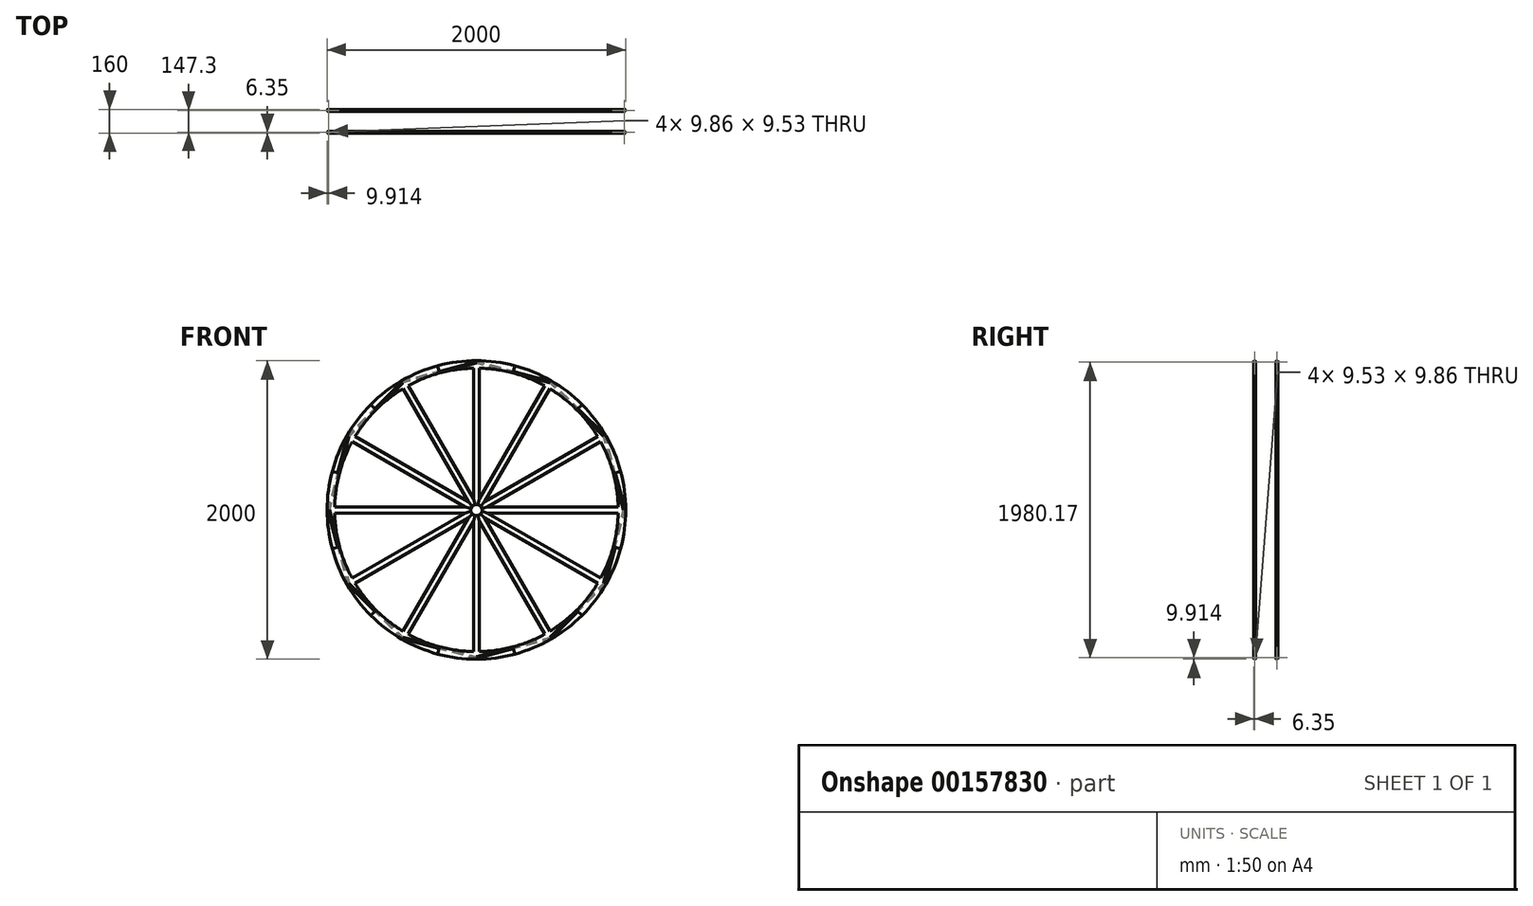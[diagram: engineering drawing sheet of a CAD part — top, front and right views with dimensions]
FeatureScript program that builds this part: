
annotation { "Feature Type Name" : "Feature", "Feature Type Description" : "" }
export const myFeature = defineFeature(function(context is Context, id is Id, definition is map)
    precondition{}
    {
        {
            var Q0;
            Q0=qCreatedBy(makeId("Front.planeOp"),FACE);
            var sketch = newSketch(context, id + "F0", { "sketchPlane" : qUnion([Q0])});
            skLineSegment(sketch, "E0", {"start": v(0, 0) * mm, "end": v(1000, 0) * mm, "construction": true});
            skCircle(sketch, "E1", {"center": v(0, 0) * mm, "radius": 1000 * mm, "construction": true});
            skLineSegment(sketch, "E2", {"start": v(0, 0) * mm, "end": v(965.93, 258.82) * mm, "construction": true});
            skCircle(sketch, "E3", {"center": v(0, 0) * mm, "radius": 77.27 * mm, "construction": true});
            skLineSegment(sketch, "E4", {"start": v(37.32, 10) * mm, "end": v(37.32, 0) * mm});
            skLineSegment(sketch, "E5", {"start": v(37.32, 10) * mm, "end": v(74.64, 20) * mm});
            skLineSegment(sketch, "E6", {"start": v(74.64, 20) * mm, "end": v(949.79, 20) * mm});
            skArc(sketch, "E7", {"start": v(1000, 0) * mm, "mid": v(991.44, 130.53) * mm, "end": v(965.93, 258.82) * mm});
            skArc(sketch, "E8", {"start": v(949.79, 20) * mm, "mid": v(940.52, 133.9) * mm, "end": v(917.63, 245.88) * mm});
            skLineSegment(sketch, "E9", {"start": v(917.63, 245.88) * mm, "end": v(965.93, 258.82) * mm});
            skArc(sketch, "E10.MirrorCS", {"start": v(1000, 0) * mm, "mid": v(991.44, -130.53) * mm, "end": v(965.93, -258.82) * mm});
            skLineSegment(sketch, "E11.MirrorCS", {"start": v(917.63, -245.88) * mm, "end": v(965.93, -258.82) * mm});
            skArc(sketch, "E12.MirrorCS", {"start": v(949.79, -20) * mm, "mid": v(940.52, -133.9) * mm, "end": v(917.63, -245.88) * mm});
            skLineSegment(sketch, "E13.MirrorCS", {"start": v(74.64, -20) * mm, "end": v(949.79, -20) * mm});
            skLineSegment(sketch, "E14.MirrorCS", {"start": v(37.32, -10) * mm, "end": v(37.32, 0) * mm});
            skLineSegment(sketch, "E15.MirrorCS", {"start": v(37.32, -10) * mm, "end": v(74.64, -20) * mm});
            skSolve(sketch);
        }
        {
            var Q0;
            Q0=makeQuery(id+"F0.imprint","IMPRINT",FACE,{"disambiguationData":[TD([[makeQuery(id+"F0.imprint","IMPRINT",EDGE,{"derivedFrom":sQuery(id+"F0.wireOp",EDGE,"E4")}),1.0]])]});
            extrude(context, id + "F1", {"entities" : qUnion([Q0]), "depth" : 1 / 406.4 * mm});
        }
        {
            var Q0;
            Q0=qCreatedBy(makeId("Right.planeOp"),FACE);
            var sketch = newSketch(context, id + "F2", { "sketchPlane" : qUnion([Q0])});
            skLineSegment(sketch, "E16", {"start": v(0, 0) * mm, "end": v(504.9, 0) * mm, "construction": true});
            skSolve(sketch);
        }
        {
            var Q0;
            Q0=sQuery(id+"F0.wireOp",VERTEX,"E7.end");
            var Q1;
            Q1=sQuery(id+"F0.wireOp",EDGE,"E1");
            cPlane(context, id + "F3", {"entities" : qUnion([Q0, Q1]), "cplaneType" : CPlaneType.CURVE_POINT, "offset" : 25 * mm, "width" : 150 * mm, "height" : 150 * mm});
        }
        {
            var Q0;
            Q0=qCreatedBy(id+"F3.planeOp",FACE);
            var sketch = newSketch(context, id + "F4", { "sketchPlane" : qUnion([Q0])});
            skLineSegment(sketch, "E17.bottom", {"start": v(950.5, 0) * mm, "end": v(962.2, 0) * mm});
            skLineSegment(sketch, "E17.top", {"start": v(950.5, 12.7) * mm, "end": v(962.2, 12.7) * mm});
            skLineSegment(sketch, "E17.left", {"start": v(950, 0.5) * mm, "end": v(950, 12.2) * mm});
            skLineSegment(sketch, "E17.right", {"start": v(962.7, 0.5) * mm, "end": v(962.7, 12.2) * mm});
            skLineSegment(sketch, "E18.0", {"start": v(951.59, 1.59) * mm, "end": v(951.59, 11.11) * mm});
            skLineSegment(sketch, "E18.1", {"start": v(951.59, 1.59) * mm, "end": v(961.11, 1.59) * mm});
            skLineSegment(sketch, "E18.2", {"start": v(961.11, 1.59) * mm, "end": v(961.11, 11.11) * mm});
            skLineSegment(sketch, "E18.3", {"start": v(951.59, 11.11) * mm, "end": v(961.11, 11.11) * mm});
            skPoint(sketch, "E19.visualSharp", {"position": v(950, 12.7) * mm});
            skArc(sketch, "E19.filletArc", {"start": v(950.5, 12.7) * mm, "mid": v(950.15, 12.55) * mm, "end": v(950, 12.2) * mm});
            skPoint(sketch, "E20.visualSharp", {"position": v(962.7, 12.7) * mm});
            skArc(sketch, "E20.filletArc", {"start": v(962.7, 12.2) * mm, "mid": v(962.55, 12.55) * mm, "end": v(962.2, 12.7) * mm});
            skPoint(sketch, "E21.visualSharp", {"position": v(962.7, 0) * mm});
            skArc(sketch, "E21.filletArc", {"start": v(962.2, 0) * mm, "mid": v(962.55, 0.15) * mm, "end": v(962.7, 0.5) * mm});
            skPoint(sketch, "E22.visualSharp", {"position": v(950, 0) * mm});
            skArc(sketch, "E22.filletArc", {"start": v(950, 0.5) * mm, "mid": v(950.15, 0.15) * mm, "end": v(950.5, 0) * mm});
            skSolve(sketch);
        }
        {
            var Q0;
            Q0 = qSketchRegion(id + "F4", true);
            var Q1;
            Q1=qCreatedBy(makeId("Top.planeOp"),FACE);
            extrude(context, id + "F5", {"entities" : qUnion([Q0]), "endBound" : BoundingType.UP_TO_SURFACE, "oppositeDirection" : true, "endBoundEntityFace" : qUnion([Q1]), "depth" : 25 * mm});
        }
        {
            var Q0;
            Q0=makeQuery(id+"F5.opExtrude","SWEPT_BODY",BODY,{"disambiguationData":[OSD([sQuery(id+"F4.wireOp",EDGE,"E17.bottom"),sQuery(id+"F4.wireOp",EDGE,"E17.top"),sQuery(id+"F4.wireOp",EDGE,"E17.left"),sQuery(id+"F4.wireOp",EDGE,"E17.right"),sQuery(id+"F4.wireOp",EDGE,"E18.0"),sQuery(id+"F4.wireOp",EDGE,"E18.1"),sQuery(id+"F4.wireOp",EDGE,"E18.2"),sQuery(id+"F4.wireOp",EDGE,"E18.3"),sQuery(id+"F4.wireOp",EDGE,"E19.filletArc"),sQuery(id+"F4.wireOp",EDGE,"E20.filletArc"),sQuery(id+"F4.wireOp",EDGE,"E21.filletArc"),sQuery(id+"F4.wireOp",EDGE,"E22.filletArc")])]});
            var Q1;
            Q1=qCreatedBy(id+"F3.planeOp",FACE);
            mirror(context, id + "F6", {"operationType" : NewBodyOperationType.ADD, "entities" : qUnion([Q0]), "mirrorPlane" : qUnion([Q1])});
        }
        {
            var Q0;
            Q0=makeQuery(id+"F1.opExtrude","SWEPT_BODY",BODY,{"disambiguationData":[OSD([sQuery(id+"F0.wireOp",EDGE,"E4"),sQuery(id+"F0.wireOp",EDGE,"E5"),sQuery(id+"F0.wireOp",EDGE,"E6"),sQuery(id+"F0.wireOp",EDGE,"E7"),sQuery(id+"F0.wireOp",EDGE,"E8"),sQuery(id+"F0.wireOp",EDGE,"E9"),sQuery(id+"F0.wireOp",EDGE,"E10.MirrorCS"),sQuery(id+"F0.wireOp",EDGE,"E11.MirrorCS"),sQuery(id+"F0.wireOp",EDGE,"E12.MirrorCS"),sQuery(id+"F0.wireOp",EDGE,"E13.MirrorCS"),sQuery(id+"F0.wireOp",EDGE,"E14.MirrorCS"),sQuery(id+"F0.wireOp",EDGE,"E15.MirrorCS")])]});
            var Q1;
            Q1=makeQuery(id+"F5.opExtrude","SWEPT_BODY",BODY,{"disambiguationData":[OSD([sQuery(id+"F4.wireOp",EDGE,"E17.bottom"),sQuery(id+"F4.wireOp",EDGE,"E17.top"),sQuery(id+"F4.wireOp",EDGE,"E17.left"),sQuery(id+"F4.wireOp",EDGE,"E17.right"),sQuery(id+"F4.wireOp",EDGE,"E18.0"),sQuery(id+"F4.wireOp",EDGE,"E18.1"),sQuery(id+"F4.wireOp",EDGE,"E18.2"),sQuery(id+"F4.wireOp",EDGE,"E18.3"),sQuery(id+"F4.wireOp",EDGE,"E19.filletArc"),sQuery(id+"F4.wireOp",EDGE,"E20.filletArc"),sQuery(id+"F4.wireOp",EDGE,"E21.filletArc"),sQuery(id+"F4.wireOp",EDGE,"E22.filletArc")])]});
            var Q2;
            Q2=sQuery(id+"F2.wireOp",EDGE,"E16");
            circularPattern(context, id + "F7", {"entities" : qUnion([Q0, Q1]), "axis" : qUnion([Q2]), "angle" : 30 * degree, "instanceCount" : 12});
        }
        {
            var Q0;
            Q0=qCreatedBy(makeId("Front.planeOp"),FACE);
            cPlane(context, id + "F8", {"entities" : qUnion([Q0]), "cplaneType" : CPlaneType.OFFSET, "offset" : 80 * mm, "oppositeDirection" : true, "width" : 150 * mm, "height" : 150 * mm});
        }
        {
            var Q0;
            Q0=makeQuery(id+"F1.opExtrude","SWEPT_BODY",BODY,{"disambiguationData":[OSD([sQuery(id+"F0.wireOp",EDGE,"E4"),sQuery(id+"F0.wireOp",EDGE,"E5"),sQuery(id+"F0.wireOp",EDGE,"E6"),sQuery(id+"F0.wireOp",EDGE,"E7"),sQuery(id+"F0.wireOp",EDGE,"E8"),sQuery(id+"F0.wireOp",EDGE,"E9"),sQuery(id+"F0.wireOp",EDGE,"E10.MirrorCS"),sQuery(id+"F0.wireOp",EDGE,"E11.MirrorCS"),sQuery(id+"F0.wireOp",EDGE,"E12.MirrorCS"),sQuery(id+"F0.wireOp",EDGE,"E13.MirrorCS"),sQuery(id+"F0.wireOp",EDGE,"E14.MirrorCS"),sQuery(id+"F0.wireOp",EDGE,"E15.MirrorCS")])]});
            var Q1;
            Q1=makeQuery(id+"F5.opExtrude","SWEPT_BODY",BODY,{"disambiguationData":[OSD([sQuery(id+"F4.wireOp",EDGE,"E17.bottom"),sQuery(id+"F4.wireOp",EDGE,"E17.top"),sQuery(id+"F4.wireOp",EDGE,"E17.left"),sQuery(id+"F4.wireOp",EDGE,"E17.right"),sQuery(id+"F4.wireOp",EDGE,"E18.0"),sQuery(id+"F4.wireOp",EDGE,"E18.1"),sQuery(id+"F4.wireOp",EDGE,"E18.2"),sQuery(id+"F4.wireOp",EDGE,"E18.3"),sQuery(id+"F4.wireOp",EDGE,"E19.filletArc"),sQuery(id+"F4.wireOp",EDGE,"E20.filletArc"),sQuery(id+"F4.wireOp",EDGE,"E21.filletArc"),sQuery(id+"F4.wireOp",EDGE,"E22.filletArc")])]});
            var Q2;
            Q2=makeQuery(id+"F7.opPattern","COPY",BODY,{"derivedFrom":makeQuery(id+"F1.opExtrude","SWEPT_BODY",BODY,{"disambiguationData":[OSD([sQuery(id+"F0.wireOp",EDGE,"E4"),sQuery(id+"F0.wireOp",EDGE,"E5"),sQuery(id+"F0.wireOp",EDGE,"E6"),sQuery(id+"F0.wireOp",EDGE,"E7"),sQuery(id+"F0.wireOp",EDGE,"E8"),sQuery(id+"F0.wireOp",EDGE,"E9"),sQuery(id+"F0.wireOp",EDGE,"E10.MirrorCS"),sQuery(id+"F0.wireOp",EDGE,"E11.MirrorCS"),sQuery(id+"F0.wireOp",EDGE,"E12.MirrorCS"),sQuery(id+"F0.wireOp",EDGE,"E13.MirrorCS"),sQuery(id+"F0.wireOp",EDGE,"E14.MirrorCS"),sQuery(id+"F0.wireOp",EDGE,"E15.MirrorCS")])]}),"instanceName":"1"});
            var Q3;
            Q3=makeQuery(id+"F7.opPattern","COPY",BODY,{"derivedFrom":makeQuery(id+"F5.opExtrude","SWEPT_BODY",BODY,{"disambiguationData":[OSD([sQuery(id+"F4.wireOp",EDGE,"E17.bottom"),sQuery(id+"F4.wireOp",EDGE,"E17.top"),sQuery(id+"F4.wireOp",EDGE,"E17.left"),sQuery(id+"F4.wireOp",EDGE,"E17.right"),sQuery(id+"F4.wireOp",EDGE,"E18.0"),sQuery(id+"F4.wireOp",EDGE,"E18.1"),sQuery(id+"F4.wireOp",EDGE,"E18.2"),sQuery(id+"F4.wireOp",EDGE,"E18.3"),sQuery(id+"F4.wireOp",EDGE,"E19.filletArc"),sQuery(id+"F4.wireOp",EDGE,"E20.filletArc"),sQuery(id+"F4.wireOp",EDGE,"E21.filletArc"),sQuery(id+"F4.wireOp",EDGE,"E22.filletArc")])]}),"instanceName":"1"});
            var Q4;
            Q4=makeQuery(id+"F7.opPattern","COPY",BODY,{"derivedFrom":makeQuery(id+"F1.opExtrude","SWEPT_BODY",BODY,{"disambiguationData":[OSD([sQuery(id+"F0.wireOp",EDGE,"E4"),sQuery(id+"F0.wireOp",EDGE,"E5"),sQuery(id+"F0.wireOp",EDGE,"E6"),sQuery(id+"F0.wireOp",EDGE,"E7"),sQuery(id+"F0.wireOp",EDGE,"E8"),sQuery(id+"F0.wireOp",EDGE,"E9"),sQuery(id+"F0.wireOp",EDGE,"E10.MirrorCS"),sQuery(id+"F0.wireOp",EDGE,"E11.MirrorCS"),sQuery(id+"F0.wireOp",EDGE,"E12.MirrorCS"),sQuery(id+"F0.wireOp",EDGE,"E13.MirrorCS"),sQuery(id+"F0.wireOp",EDGE,"E14.MirrorCS"),sQuery(id+"F0.wireOp",EDGE,"E15.MirrorCS")])]}),"instanceName":"2"});
            var Q5;
            Q5=makeQuery(id+"F7.opPattern","COPY",BODY,{"derivedFrom":makeQuery(id+"F5.opExtrude","SWEPT_BODY",BODY,{"disambiguationData":[OSD([sQuery(id+"F4.wireOp",EDGE,"E17.bottom"),sQuery(id+"F4.wireOp",EDGE,"E17.top"),sQuery(id+"F4.wireOp",EDGE,"E17.left"),sQuery(id+"F4.wireOp",EDGE,"E17.right"),sQuery(id+"F4.wireOp",EDGE,"E18.0"),sQuery(id+"F4.wireOp",EDGE,"E18.1"),sQuery(id+"F4.wireOp",EDGE,"E18.2"),sQuery(id+"F4.wireOp",EDGE,"E18.3"),sQuery(id+"F4.wireOp",EDGE,"E19.filletArc"),sQuery(id+"F4.wireOp",EDGE,"E20.filletArc"),sQuery(id+"F4.wireOp",EDGE,"E21.filletArc"),sQuery(id+"F4.wireOp",EDGE,"E22.filletArc")])]}),"instanceName":"2"});
            var Q6;
            Q6=makeQuery(id+"F7.opPattern","COPY",BODY,{"derivedFrom":makeQuery(id+"F1.opExtrude","SWEPT_BODY",BODY,{"disambiguationData":[OSD([sQuery(id+"F0.wireOp",EDGE,"E4"),sQuery(id+"F0.wireOp",EDGE,"E5"),sQuery(id+"F0.wireOp",EDGE,"E6"),sQuery(id+"F0.wireOp",EDGE,"E7"),sQuery(id+"F0.wireOp",EDGE,"E8"),sQuery(id+"F0.wireOp",EDGE,"E9"),sQuery(id+"F0.wireOp",EDGE,"E10.MirrorCS"),sQuery(id+"F0.wireOp",EDGE,"E11.MirrorCS"),sQuery(id+"F0.wireOp",EDGE,"E12.MirrorCS"),sQuery(id+"F0.wireOp",EDGE,"E13.MirrorCS"),sQuery(id+"F0.wireOp",EDGE,"E14.MirrorCS"),sQuery(id+"F0.wireOp",EDGE,"E15.MirrorCS")])]}),"instanceName":"3"});
            var Q7;
            Q7=makeQuery(id+"F7.opPattern","COPY",BODY,{"derivedFrom":makeQuery(id+"F5.opExtrude","SWEPT_BODY",BODY,{"disambiguationData":[OSD([sQuery(id+"F4.wireOp",EDGE,"E17.bottom"),sQuery(id+"F4.wireOp",EDGE,"E17.top"),sQuery(id+"F4.wireOp",EDGE,"E17.left"),sQuery(id+"F4.wireOp",EDGE,"E17.right"),sQuery(id+"F4.wireOp",EDGE,"E18.0"),sQuery(id+"F4.wireOp",EDGE,"E18.1"),sQuery(id+"F4.wireOp",EDGE,"E18.2"),sQuery(id+"F4.wireOp",EDGE,"E18.3"),sQuery(id+"F4.wireOp",EDGE,"E19.filletArc"),sQuery(id+"F4.wireOp",EDGE,"E20.filletArc"),sQuery(id+"F4.wireOp",EDGE,"E21.filletArc"),sQuery(id+"F4.wireOp",EDGE,"E22.filletArc")])]}),"instanceName":"3"});
            var Q8;
            Q8=makeQuery(id+"F7.opPattern","COPY",BODY,{"derivedFrom":makeQuery(id+"F1.opExtrude","SWEPT_BODY",BODY,{"disambiguationData":[OSD([sQuery(id+"F0.wireOp",EDGE,"E4"),sQuery(id+"F0.wireOp",EDGE,"E5"),sQuery(id+"F0.wireOp",EDGE,"E6"),sQuery(id+"F0.wireOp",EDGE,"E7"),sQuery(id+"F0.wireOp",EDGE,"E8"),sQuery(id+"F0.wireOp",EDGE,"E9"),sQuery(id+"F0.wireOp",EDGE,"E10.MirrorCS"),sQuery(id+"F0.wireOp",EDGE,"E11.MirrorCS"),sQuery(id+"F0.wireOp",EDGE,"E12.MirrorCS"),sQuery(id+"F0.wireOp",EDGE,"E13.MirrorCS"),sQuery(id+"F0.wireOp",EDGE,"E14.MirrorCS"),sQuery(id+"F0.wireOp",EDGE,"E15.MirrorCS")])]}),"instanceName":"4"});
            var Q9;
            Q9=makeQuery(id+"F7.opPattern","COPY",BODY,{"derivedFrom":makeQuery(id+"F5.opExtrude","SWEPT_BODY",BODY,{"disambiguationData":[OSD([sQuery(id+"F4.wireOp",EDGE,"E17.bottom"),sQuery(id+"F4.wireOp",EDGE,"E17.top"),sQuery(id+"F4.wireOp",EDGE,"E17.left"),sQuery(id+"F4.wireOp",EDGE,"E17.right"),sQuery(id+"F4.wireOp",EDGE,"E18.0"),sQuery(id+"F4.wireOp",EDGE,"E18.1"),sQuery(id+"F4.wireOp",EDGE,"E18.2"),sQuery(id+"F4.wireOp",EDGE,"E18.3"),sQuery(id+"F4.wireOp",EDGE,"E19.filletArc"),sQuery(id+"F4.wireOp",EDGE,"E20.filletArc"),sQuery(id+"F4.wireOp",EDGE,"E21.filletArc"),sQuery(id+"F4.wireOp",EDGE,"E22.filletArc")])]}),"instanceName":"4"});
            var Q10;
            Q10=makeQuery(id+"F7.opPattern","COPY",BODY,{"derivedFrom":makeQuery(id+"F1.opExtrude","SWEPT_BODY",BODY,{"disambiguationData":[OSD([sQuery(id+"F0.wireOp",EDGE,"E4"),sQuery(id+"F0.wireOp",EDGE,"E5"),sQuery(id+"F0.wireOp",EDGE,"E6"),sQuery(id+"F0.wireOp",EDGE,"E7"),sQuery(id+"F0.wireOp",EDGE,"E8"),sQuery(id+"F0.wireOp",EDGE,"E9"),sQuery(id+"F0.wireOp",EDGE,"E10.MirrorCS"),sQuery(id+"F0.wireOp",EDGE,"E11.MirrorCS"),sQuery(id+"F0.wireOp",EDGE,"E12.MirrorCS"),sQuery(id+"F0.wireOp",EDGE,"E13.MirrorCS"),sQuery(id+"F0.wireOp",EDGE,"E14.MirrorCS"),sQuery(id+"F0.wireOp",EDGE,"E15.MirrorCS")])]}),"instanceName":"5"});
            var Q11;
            Q11=makeQuery(id+"F7.opPattern","COPY",BODY,{"derivedFrom":makeQuery(id+"F5.opExtrude","SWEPT_BODY",BODY,{"disambiguationData":[OSD([sQuery(id+"F4.wireOp",EDGE,"E17.bottom"),sQuery(id+"F4.wireOp",EDGE,"E17.top"),sQuery(id+"F4.wireOp",EDGE,"E17.left"),sQuery(id+"F4.wireOp",EDGE,"E17.right"),sQuery(id+"F4.wireOp",EDGE,"E18.0"),sQuery(id+"F4.wireOp",EDGE,"E18.1"),sQuery(id+"F4.wireOp",EDGE,"E18.2"),sQuery(id+"F4.wireOp",EDGE,"E18.3"),sQuery(id+"F4.wireOp",EDGE,"E19.filletArc"),sQuery(id+"F4.wireOp",EDGE,"E20.filletArc"),sQuery(id+"F4.wireOp",EDGE,"E21.filletArc"),sQuery(id+"F4.wireOp",EDGE,"E22.filletArc")])]}),"instanceName":"5"});
            var Q12;
            Q12=makeQuery(id+"F7.opPattern","COPY",BODY,{"derivedFrom":makeQuery(id+"F1.opExtrude","SWEPT_BODY",BODY,{"disambiguationData":[OSD([sQuery(id+"F0.wireOp",EDGE,"E4"),sQuery(id+"F0.wireOp",EDGE,"E5"),sQuery(id+"F0.wireOp",EDGE,"E6"),sQuery(id+"F0.wireOp",EDGE,"E7"),sQuery(id+"F0.wireOp",EDGE,"E8"),sQuery(id+"F0.wireOp",EDGE,"E9"),sQuery(id+"F0.wireOp",EDGE,"E10.MirrorCS"),sQuery(id+"F0.wireOp",EDGE,"E11.MirrorCS"),sQuery(id+"F0.wireOp",EDGE,"E12.MirrorCS"),sQuery(id+"F0.wireOp",EDGE,"E13.MirrorCS"),sQuery(id+"F0.wireOp",EDGE,"E14.MirrorCS"),sQuery(id+"F0.wireOp",EDGE,"E15.MirrorCS")])]}),"instanceName":"6"});
            var Q13;
            Q13=makeQuery(id+"F7.opPattern","COPY",BODY,{"derivedFrom":makeQuery(id+"F5.opExtrude","SWEPT_BODY",BODY,{"disambiguationData":[OSD([sQuery(id+"F4.wireOp",EDGE,"E17.bottom"),sQuery(id+"F4.wireOp",EDGE,"E17.top"),sQuery(id+"F4.wireOp",EDGE,"E17.left"),sQuery(id+"F4.wireOp",EDGE,"E17.right"),sQuery(id+"F4.wireOp",EDGE,"E18.0"),sQuery(id+"F4.wireOp",EDGE,"E18.1"),sQuery(id+"F4.wireOp",EDGE,"E18.2"),sQuery(id+"F4.wireOp",EDGE,"E18.3"),sQuery(id+"F4.wireOp",EDGE,"E19.filletArc"),sQuery(id+"F4.wireOp",EDGE,"E20.filletArc"),sQuery(id+"F4.wireOp",EDGE,"E21.filletArc"),sQuery(id+"F4.wireOp",EDGE,"E22.filletArc")])]}),"instanceName":"6"});
            var Q14;
            Q14=makeQuery(id+"F7.opPattern","COPY",BODY,{"derivedFrom":makeQuery(id+"F1.opExtrude","SWEPT_BODY",BODY,{"disambiguationData":[OSD([sQuery(id+"F0.wireOp",EDGE,"E4"),sQuery(id+"F0.wireOp",EDGE,"E5"),sQuery(id+"F0.wireOp",EDGE,"E6"),sQuery(id+"F0.wireOp",EDGE,"E7"),sQuery(id+"F0.wireOp",EDGE,"E8"),sQuery(id+"F0.wireOp",EDGE,"E9"),sQuery(id+"F0.wireOp",EDGE,"E10.MirrorCS"),sQuery(id+"F0.wireOp",EDGE,"E11.MirrorCS"),sQuery(id+"F0.wireOp",EDGE,"E12.MirrorCS"),sQuery(id+"F0.wireOp",EDGE,"E13.MirrorCS"),sQuery(id+"F0.wireOp",EDGE,"E14.MirrorCS"),sQuery(id+"F0.wireOp",EDGE,"E15.MirrorCS")])]}),"instanceName":"7"});
            var Q15;
            Q15=makeQuery(id+"F7.opPattern","COPY",BODY,{"derivedFrom":makeQuery(id+"F5.opExtrude","SWEPT_BODY",BODY,{"disambiguationData":[OSD([sQuery(id+"F4.wireOp",EDGE,"E17.bottom"),sQuery(id+"F4.wireOp",EDGE,"E17.top"),sQuery(id+"F4.wireOp",EDGE,"E17.left"),sQuery(id+"F4.wireOp",EDGE,"E17.right"),sQuery(id+"F4.wireOp",EDGE,"E18.0"),sQuery(id+"F4.wireOp",EDGE,"E18.1"),sQuery(id+"F4.wireOp",EDGE,"E18.2"),sQuery(id+"F4.wireOp",EDGE,"E18.3"),sQuery(id+"F4.wireOp",EDGE,"E19.filletArc"),sQuery(id+"F4.wireOp",EDGE,"E20.filletArc"),sQuery(id+"F4.wireOp",EDGE,"E21.filletArc"),sQuery(id+"F4.wireOp",EDGE,"E22.filletArc")])]}),"instanceName":"7"});
            var Q16;
            Q16=makeQuery(id+"F7.opPattern","COPY",BODY,{"derivedFrom":makeQuery(id+"F1.opExtrude","SWEPT_BODY",BODY,{"disambiguationData":[OSD([sQuery(id+"F0.wireOp",EDGE,"E4"),sQuery(id+"F0.wireOp",EDGE,"E5"),sQuery(id+"F0.wireOp",EDGE,"E6"),sQuery(id+"F0.wireOp",EDGE,"E7"),sQuery(id+"F0.wireOp",EDGE,"E8"),sQuery(id+"F0.wireOp",EDGE,"E9"),sQuery(id+"F0.wireOp",EDGE,"E10.MirrorCS"),sQuery(id+"F0.wireOp",EDGE,"E11.MirrorCS"),sQuery(id+"F0.wireOp",EDGE,"E12.MirrorCS"),sQuery(id+"F0.wireOp",EDGE,"E13.MirrorCS"),sQuery(id+"F0.wireOp",EDGE,"E14.MirrorCS"),sQuery(id+"F0.wireOp",EDGE,"E15.MirrorCS")])]}),"instanceName":"8"});
            var Q17;
            Q17=makeQuery(id+"F7.opPattern","COPY",BODY,{"derivedFrom":makeQuery(id+"F5.opExtrude","SWEPT_BODY",BODY,{"disambiguationData":[OSD([sQuery(id+"F4.wireOp",EDGE,"E17.bottom"),sQuery(id+"F4.wireOp",EDGE,"E17.top"),sQuery(id+"F4.wireOp",EDGE,"E17.left"),sQuery(id+"F4.wireOp",EDGE,"E17.right"),sQuery(id+"F4.wireOp",EDGE,"E18.0"),sQuery(id+"F4.wireOp",EDGE,"E18.1"),sQuery(id+"F4.wireOp",EDGE,"E18.2"),sQuery(id+"F4.wireOp",EDGE,"E18.3"),sQuery(id+"F4.wireOp",EDGE,"E19.filletArc"),sQuery(id+"F4.wireOp",EDGE,"E20.filletArc"),sQuery(id+"F4.wireOp",EDGE,"E21.filletArc"),sQuery(id+"F4.wireOp",EDGE,"E22.filletArc")])]}),"instanceName":"8"});
            var Q18;
            Q18=makeQuery(id+"F7.opPattern","COPY",BODY,{"derivedFrom":makeQuery(id+"F1.opExtrude","SWEPT_BODY",BODY,{"disambiguationData":[OSD([sQuery(id+"F0.wireOp",EDGE,"E4"),sQuery(id+"F0.wireOp",EDGE,"E5"),sQuery(id+"F0.wireOp",EDGE,"E6"),sQuery(id+"F0.wireOp",EDGE,"E7"),sQuery(id+"F0.wireOp",EDGE,"E8"),sQuery(id+"F0.wireOp",EDGE,"E9"),sQuery(id+"F0.wireOp",EDGE,"E10.MirrorCS"),sQuery(id+"F0.wireOp",EDGE,"E11.MirrorCS"),sQuery(id+"F0.wireOp",EDGE,"E12.MirrorCS"),sQuery(id+"F0.wireOp",EDGE,"E13.MirrorCS"),sQuery(id+"F0.wireOp",EDGE,"E14.MirrorCS"),sQuery(id+"F0.wireOp",EDGE,"E15.MirrorCS")])]}),"instanceName":"9"});
            var Q19;
            Q19=makeQuery(id+"F7.opPattern","COPY",BODY,{"derivedFrom":makeQuery(id+"F5.opExtrude","SWEPT_BODY",BODY,{"disambiguationData":[OSD([sQuery(id+"F4.wireOp",EDGE,"E17.bottom"),sQuery(id+"F4.wireOp",EDGE,"E17.top"),sQuery(id+"F4.wireOp",EDGE,"E17.left"),sQuery(id+"F4.wireOp",EDGE,"E17.right"),sQuery(id+"F4.wireOp",EDGE,"E18.0"),sQuery(id+"F4.wireOp",EDGE,"E18.1"),sQuery(id+"F4.wireOp",EDGE,"E18.2"),sQuery(id+"F4.wireOp",EDGE,"E18.3"),sQuery(id+"F4.wireOp",EDGE,"E19.filletArc"),sQuery(id+"F4.wireOp",EDGE,"E20.filletArc"),sQuery(id+"F4.wireOp",EDGE,"E21.filletArc"),sQuery(id+"F4.wireOp",EDGE,"E22.filletArc")])]}),"instanceName":"9"});
            var Q20;
            Q20=makeQuery(id+"F7.opPattern","COPY",BODY,{"derivedFrom":makeQuery(id+"F1.opExtrude","SWEPT_BODY",BODY,{"disambiguationData":[OSD([sQuery(id+"F0.wireOp",EDGE,"E4"),sQuery(id+"F0.wireOp",EDGE,"E5"),sQuery(id+"F0.wireOp",EDGE,"E6"),sQuery(id+"F0.wireOp",EDGE,"E7"),sQuery(id+"F0.wireOp",EDGE,"E8"),sQuery(id+"F0.wireOp",EDGE,"E9"),sQuery(id+"F0.wireOp",EDGE,"E10.MirrorCS"),sQuery(id+"F0.wireOp",EDGE,"E11.MirrorCS"),sQuery(id+"F0.wireOp",EDGE,"E12.MirrorCS"),sQuery(id+"F0.wireOp",EDGE,"E13.MirrorCS"),sQuery(id+"F0.wireOp",EDGE,"E14.MirrorCS"),sQuery(id+"F0.wireOp",EDGE,"E15.MirrorCS")])]}),"instanceName":"10"});
            var Q21;
            Q21=makeQuery(id+"F7.opPattern","COPY",BODY,{"derivedFrom":makeQuery(id+"F5.opExtrude","SWEPT_BODY",BODY,{"disambiguationData":[OSD([sQuery(id+"F4.wireOp",EDGE,"E17.bottom"),sQuery(id+"F4.wireOp",EDGE,"E17.top"),sQuery(id+"F4.wireOp",EDGE,"E17.left"),sQuery(id+"F4.wireOp",EDGE,"E17.right"),sQuery(id+"F4.wireOp",EDGE,"E18.0"),sQuery(id+"F4.wireOp",EDGE,"E18.1"),sQuery(id+"F4.wireOp",EDGE,"E18.2"),sQuery(id+"F4.wireOp",EDGE,"E18.3"),sQuery(id+"F4.wireOp",EDGE,"E19.filletArc"),sQuery(id+"F4.wireOp",EDGE,"E20.filletArc"),sQuery(id+"F4.wireOp",EDGE,"E21.filletArc"),sQuery(id+"F4.wireOp",EDGE,"E22.filletArc")])]}),"instanceName":"10"});
            var Q22;
            Q22=makeQuery(id+"F7.opPattern","COPY",BODY,{"derivedFrom":makeQuery(id+"F1.opExtrude","SWEPT_BODY",BODY,{"disambiguationData":[OSD([sQuery(id+"F0.wireOp",EDGE,"E4"),sQuery(id+"F0.wireOp",EDGE,"E5"),sQuery(id+"F0.wireOp",EDGE,"E6"),sQuery(id+"F0.wireOp",EDGE,"E7"),sQuery(id+"F0.wireOp",EDGE,"E8"),sQuery(id+"F0.wireOp",EDGE,"E9"),sQuery(id+"F0.wireOp",EDGE,"E10.MirrorCS"),sQuery(id+"F0.wireOp",EDGE,"E11.MirrorCS"),sQuery(id+"F0.wireOp",EDGE,"E12.MirrorCS"),sQuery(id+"F0.wireOp",EDGE,"E13.MirrorCS"),sQuery(id+"F0.wireOp",EDGE,"E14.MirrorCS"),sQuery(id+"F0.wireOp",EDGE,"E15.MirrorCS")])]}),"instanceName":"11"});
            var Q23;
            Q23=makeQuery(id+"F7.opPattern","COPY",BODY,{"derivedFrom":makeQuery(id+"F5.opExtrude","SWEPT_BODY",BODY,{"disambiguationData":[OSD([sQuery(id+"F4.wireOp",EDGE,"E17.bottom"),sQuery(id+"F4.wireOp",EDGE,"E17.top"),sQuery(id+"F4.wireOp",EDGE,"E17.left"),sQuery(id+"F4.wireOp",EDGE,"E17.right"),sQuery(id+"F4.wireOp",EDGE,"E18.0"),sQuery(id+"F4.wireOp",EDGE,"E18.1"),sQuery(id+"F4.wireOp",EDGE,"E18.2"),sQuery(id+"F4.wireOp",EDGE,"E18.3"),sQuery(id+"F4.wireOp",EDGE,"E19.filletArc"),sQuery(id+"F4.wireOp",EDGE,"E20.filletArc"),sQuery(id+"F4.wireOp",EDGE,"E21.filletArc"),sQuery(id+"F4.wireOp",EDGE,"E22.filletArc")])]}),"instanceName":"11"});
            var Q24;
            Q24=qCreatedBy(id+"F8.planeOp",FACE);
            mirror(context, id + "F9", {"entities" : qUnion([Q0, Q1, Q2, Q3, Q4, Q5, Q6, Q7, Q8, Q9, Q10, Q11, Q12, Q13, Q14, Q15, Q16, Q17, Q18, Q19, Q20, Q21, Q22, Q23]), "mirrorPlane" : qUnion([Q24])});
        }
    });
